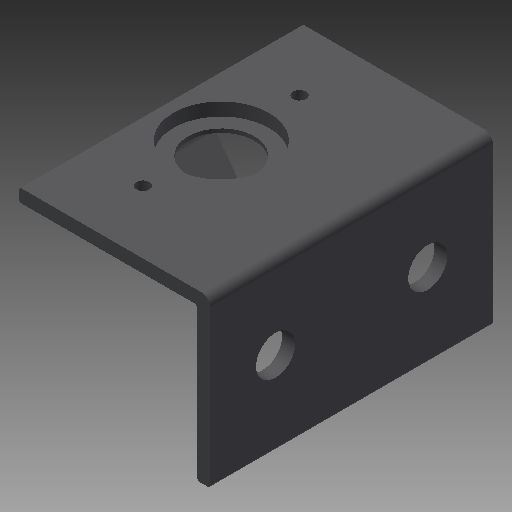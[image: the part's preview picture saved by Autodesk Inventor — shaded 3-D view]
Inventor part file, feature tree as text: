
AUTODESK INVENTOR PART (.ipt)
format: ipt  version: 2018 (Build 220112000, 112)  size: 251,392 bytes
history: native  units: mm
features: other x14, extrude x12, sketch x12
ambient origin geometry x8: Origin, YZ Plane, XZ Plane, XY Plane, X Axis, Y Axis, Z Axis, Center Point
bodies: Solid1 (feature_tree)
feature tree (38):
  extrude  "Extrusion1"  Depth=3.0mm TaperAngle=0.0deg
  extrude  "Extrusion2"  Depth=12.0mm TaperAngle=0.0deg
  extrude  "Extrusion3"  Depth=1.5mm TaperAngle=0.0deg
  extrude  "Extrusion4"  Depth=30.0mm TaperAngle=0.0deg
  extrude  "Extrusion5"  Depth=3.0mm TaperAngle=0.0deg
  extrude  "Extrusion6"  Depth=0.45mm TaperAngle=0.0deg
  extrude  "Extrusion7"  [1 undecoded]
  extrude  "Extrusion8"  [1 undecoded]
  extrude  "Extrusion9"  [1 undecoded]
  extrude  "Extrusion10"  [1 undecoded]
  extrude  "Extrusion11"  [1 undecoded]
  extrude  "Extrusion12"  [1 undecoded]
  other  "side_1_XY"
  other  "side_1_YZ"
  other  "side_1_ZX"
  other  "side_1_X"
  other  "side_1_Y"
  other  "side_1_Z"
  other  "side_1_Center"
  other  "side_2_XY"
  other  "side_2_YZ"
  other  "side_2_ZX"
  other  "side_2_X"
  other  "side_2_Y"
  other  "side_2_Z"
  other  "side_2_Center"
  sketch  "Skizze_1"  dims[d0=32.5mm d1=0.0mm d2=3.0mm d3=0.0mm]
  sketch  "Skizze_2"  dims[d8=1.94mm d9=0.0mm d10=1.5mm d11=0.0mm]
  sketch  "Skizze_3"  dims[d16=30.0mm d17=0.0mm d18=3.0mm d19=0.0mm]
  sketch  "Skizze_4"
  sketch  "Skizze_5"
  sketch  "Skizze_6_ALT_Drilling_1"  dims[d4=3.0mm d5=0.0mm d6=12.0mm d7=0.0mm]
  sketch  "Skizze_7_ALT_Drilling_2"  dims[d12=2.6mm d13=0.0mm d14=30.0mm d15=0.0mm]
  sketch  "Skizze_8"
  sketch  "Skizze_9"
  sketch  "Skizze_10_ALT_Drilling_3"  dims[d20=3.0mm d21=0.0mm d22=0.45mm d23=0.0mm]
  sketch  "Skizze_11_ALT_Drilling_4"
  sketch  "Skizze_12"
note: 6 required parameter values undecoded (feature->parameter linkage not recoverable at this tier; creation-order binding heuristic only, values carry confidence <= 0.55)
